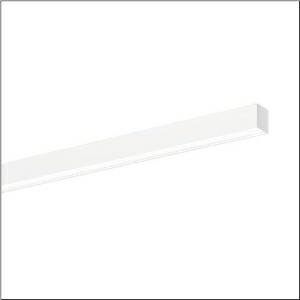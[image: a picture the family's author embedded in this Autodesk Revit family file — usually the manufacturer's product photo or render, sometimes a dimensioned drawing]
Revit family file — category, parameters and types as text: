
# Revit family: silica_r__21_51mx20da32wb_d50a
name_source: partatom
category: Lighting Fixtures
units: mm (PartAtom-declared; Revit-internal decimal feet)

## family parameters
Cut with Voids When Loaded = No
Host = Face
Light Source = No
Part Type = Normal
Room Calculation Point = No
Round Connector Dimension = Use Diameter
Shared = No

## types (1)
- --- (1 x LED, 2400 lm, 16.1 W, 3000K)
    Apparent Load = 16 VA
    CIE Flux Codes = 48 79 96 100 100
    Color Rendering = 80
    Color Temperature = 3000K
    Default Elevation = 1800 mm
    Description = Silica® 21, office luminaire, primary optical cover: cover, of PMMA, opal, light emission: direct distribution, primary light characteristic: symmetric, installation type: surface-mounted, LED, rated luminous flux: 2.400lm, luminous efficacy: 149lm/W, light colour: 830, colour temperature: 3000K, control gear: DALI 2, with terminal, 3+2-pole, max. 2.5mm², mains connection: 220..240V, AC, 50/60Hz, rated input power: 16.1W, luminaire housing, of aluminium, traffic white (RAL 9016), length: 1.204mm, width: 53mm, height: 53mm, protection rating (complete): IP20, insulation class (complete): insulation class I (protective earthing), certification: CE, permissible operating ambient temperature: 0..+35°C, standard: EN 50419, packaging unit: 1 piece
    Height = 53 mm
    Lamp = 1 x LED
    Lamp Light Flux = 2400 lm
    Lamp Power = 16.1 W
    Lamp count = 1
    Length = 1204 mm
    Luminous efficacy = 149 lm/W
    Manufacturer = Siteco
    ModVariant = No
    Model = 51MX20DA32WB
    Mounting Place = Ceiling
    Mounting Type = Surface mounted
    Number of Poles = 1
    OnlyDefault = Yes
    Power Factor = 1
    Product Name = Silica® 21
    Product group = office luminaire | ceiling mounted
    ProductGroupID = 302
    Protection Class = Protection class I
    Protection Degree = IP 20
    RLX_Detail_Level = 1
    RLX_Emergency_Light_Flux = 0 lm
    RLX_Emergency_Type = 0
    RLX_Emergency_Type_DB = No
    RlxData = <blob elided: 23785 chars, md5=f3ee9b99>
    Socket = socket
    Standby Power = 0 W
    System Light Flux = 2400 lm
    System Power = 16 W
    Type Comments = factory setting: luminous flux: 100 % | dim-lin: 254 | 233 mA
    Type Image = l_1335877.jpg
    URL = http://relux.com
    VarID = @adj_007663
    Voltage = 0 V
    Weight = 0.00 kg
    Width = 53 mm

## geometry (parser evidence)
native form markers: Blend x4, Sweep x10
no freeform markers — native parametric forms only
